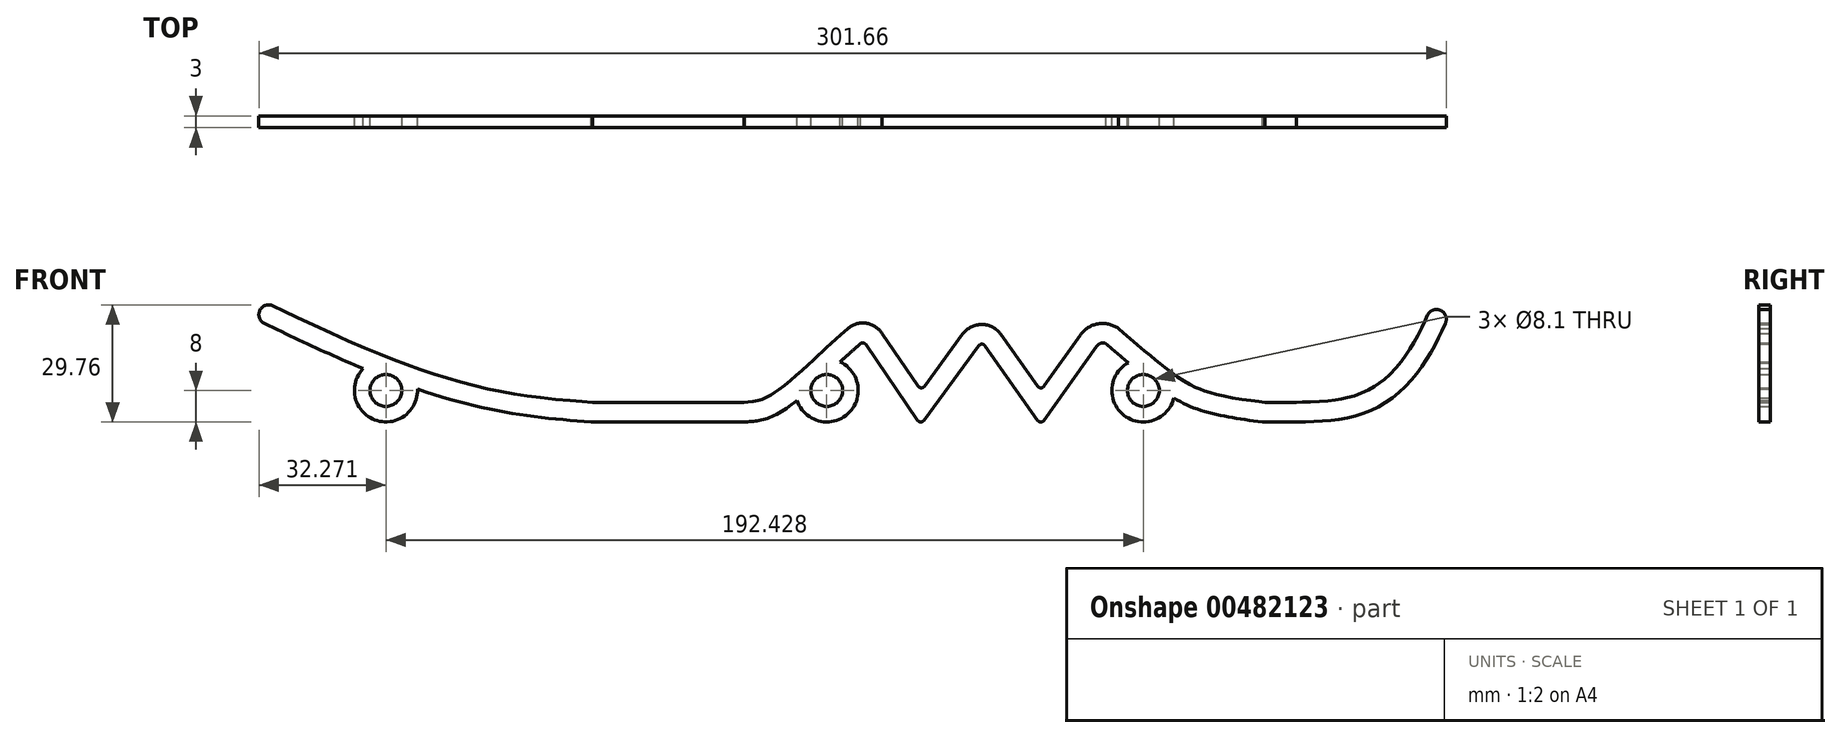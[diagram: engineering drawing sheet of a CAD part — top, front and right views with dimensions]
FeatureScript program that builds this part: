
annotation { "Feature Type Name" : "Feature", "Feature Type Description" : "" }
export const myFeature = defineFeature(function(context is Context, id is Id, definition is map)
    precondition{}
    {
        {
            var Q0;
            Q0=qCreatedBy(makeId("Front.planeOp"),FACE);
            var sketch = newSketch(context, id + "F0", { "sketchPlane" : qUnion([Q0])});
            skLineSegment(sketch, "E0.bottom", {"start": v(-221.82, -6.7) * mm, "end": v(78.18, -6.7) * mm, "construction": true});
            skLineSegment(sketch, "E0.top", {"start": v(-221.82, -36.7) * mm, "end": v(78.18, -36.7) * mm, "construction": true});
            skLineSegment(sketch, "E0.left", {"start": v(-221.82, -6.7) * mm, "end": v(-221.82, -36.7) * mm, "construction": true});
            skLineSegment(sketch, "E0.right", {"start": v(78.18, -6.7) * mm, "end": v(78.18, -36.7) * mm, "construction": true});
            skCircle(sketch, "E1", {"center": v(-190.97, -28.7) * mm, "radius": 4.05 * mm});
            skCircle(sketch, "E2", {"center": v(1.46, -28.7) * mm, "radius": 4.05 * mm});
            skLineSegment(sketch, "E3", {"start": v(-69, -17.05) * mm, "end": v(-55.9, -36.25) * mm});
            skLineSegment(sketch, "E4", {"start": v(-54.27, -36.28) * mm, "end": v(-40.4, -17.34) * mm});
            skLineSegment(sketch, "E5", {"start": v(-38.77, -17.36) * mm, "end": v(-25.39, -36.27) * mm});
            skLineSegment(sketch, "E6", {"start": v(-23.76, -36.27) * mm, "end": v(-10.46, -17.47) * mm});
            skLineSegment(sketch, "E7", {"start": v(-131.69, -16.22) * mm, "end": v(39.4, -16.22) * mm, "construction": true});
            skPoint(sketch, "E8.visualSharp", {"position": v(-99.57, -36.7) * mm});
            skPoint(sketch, "E9.visualSharp", {"position": v(-54.57, -36.7) * mm});
            skArc(sketch, "E9.filletArc", {"start": v(-55.9, -36.25) * mm, "mid": v(-55.1, -36.7) * mm, "end": v(-54.27, -36.28) * mm});
            skPoint(sketch, "E10.visualSharp", {"position": v(-24.57, -37.42) * mm});
            skArc(sketch, "E10.filletArc", {"start": v(-25.39, -36.27) * mm, "mid": v(-24.57, -36.7) * mm, "end": v(-23.76, -36.27) * mm});
            skPoint(sketch, "E11.visualSharp", {"position": v(48.18, -37.4) * mm});
            skPoint(sketch, "E12.visualSharp", {"position": v(-69.57, -16.22) * mm});
            skArc(sketch, "E12.filletArc", {"start": v(-69, -17.05) * mm, "mid": v(-69.65, -16.63) * mm, "end": v(-70.4, -16.79) * mm});
            skPoint(sketch, "E13.visualSharp", {"position": v(-39.57, -16.22) * mm});
            skArc(sketch, "E13.filletArc", {"start": v(-38.77, -17.36) * mm, "mid": v(-39.58, -16.93) * mm, "end": v(-40.4, -17.34) * mm});
            skPoint(sketch, "E14.visualSharp", {"position": v(-9.57, -16.22) * mm});
            skArc(sketch, "E14.filletArc", {"start": v(-8.14, -16.75) * mm, "mid": v(-9.42, -16.72) * mm, "end": v(-10.46, -17.47) * mm});
            skFitSpline(sketch, "E15", {"points": [v(-99.57, -36.7) * mm, v(-91.71, -34.76) * mm, v(-77.03, -22.8) * mm, v(-70.4, -16.79) * mm], "startDerivative": vector(26.04, 1.86) * mm, "endDerivative": vector(19.53, 17.39) * mm});
            skPoint(sketch, "E16", {"position": v(-221.82, -11.7) * mm});
            skFitSpline(sketch, "E17", {"points": [v(-221.82, -11.7) * mm, v(-189.76, -25.94) * mm, v(-161.24, -34.12) * mm, v(-138.8, -36.7) * mm], "startDerivative": vector(87.44, -41.7) * mm, "endDerivative": vector(74.23, -5.74) * mm});
            skLineSegment(sketch, "E18", {"start": v(-138.8, -36.7) * mm, "end": v(-99.57, -36.7) * mm});
            skFitSpline(sketch, "E19.0", {"points": [v(-219.67, -7.18) * mm, v(-216.02, -8.91) * mm, v(-208.76, -12.38) * mm, v(-199.77, -16.46) * mm, v(-192.64, -19.46) * mm, v(-187.34, -21.54) * mm, v(-182.05, -23.43) * mm, v(-176.82, -25.14) * mm, v(-171.66, -26.63) * mm, v(-166.6, -27.92) * mm, v(-161.68, -28.98) * mm, v(-156.92, -29.81) * mm, v(-152.25, -30.45) * mm, v(-146.1, -31.11) * mm, v(-141.51, -31.47) * mm, v(-138.42, -31.7) * mm]});
            skArc(sketch, "E20", {"start": v(-219.67, -7.18) * mm, "mid": v(-223, -8.36) * mm, "end": v(-221.82, -11.7) * mm});
            skFitSpline(sketch, "E21.0", {"points": [v(-99.93, -31.7) * mm, v(-99.39, -31.66) * mm, v(-98.4, -31.6) * mm, v(-97.13, -31.43) * mm, v(-96.16, -31.2) * mm, v(-95.35, -30.93) * mm, v(-94.81, -30.71) * mm, v(-94.35, -30.5) * mm, v(-94, -30.31) * mm, v(-93.62, -30.1) * mm, v(-93.07, -29.78) * mm, v(-92.33, -29.3) * mm, v(-91.05, -28.42) * mm, v(-89.33, -27.1) * mm, v(-87.18, -25.3) * mm, v(-85.02, -23.39) * mm, v(-82.93, -21.46) * mm, v(-81.29, -19.94) * mm, v(-80.07, -18.8) * mm, v(-78.93, -17.75) * mm, v(-77.63, -16.56) * mm, v(-76.24, -15.3) * mm, v(-74.95, -14.14) * mm, v(-74.13, -13.41) * mm, v(-73.72, -13.05) * mm]});
            skLineSegment(sketch, "E22", {"start": v(-138.42, -31.7) * mm, "end": v(-99.93, -31.7) * mm});
            skLineSegment(sketch, "E23.0", {"start": v(-64.88, -14.23) * mm, "end": v(-55.76, -27.6) * mm});
            skLineSegment(sketch, "E24.0", {"start": v(-34.69, -14.47) * mm, "end": v(-25.39, -27.61) * mm});
            skPoint(sketch, "E25", {"position": v(78.18, -11.7) * mm});
            skFitSpline(sketch, "E26", {"points": [v(78.18, -11.7) * mm, v(72.65, -21.98) * mm, v(63.85, -31.21) * mm, v(52.84, -35.72) * mm, v(40.46, -36.7) * mm], "startDerivative": vector(-20.1, -42.6) * mm, "endDerivative": vector(-49.74, -1.11) * mm});
            skFitSpline(sketch, "E27", {"points": [v(-8.14, -16.75) * mm, v(2.09, -25.34) * mm, v(13.73, -32.89) * mm, v(31.66, -36.7) * mm], "startDerivative": vector(32.38, -27.59) * mm, "endDerivative": vector(52.08, -6.85) * mm});
            skLineSegment(sketch, "E28", {"start": v(31.66, -36.7) * mm, "end": v(40.46, -36.7) * mm});
            skFitSpline(sketch, "E29.0", {"points": [v(-4.9, -12.94) * mm, v(-3.54, -14.1) * mm, v(-1.53, -15.81) * mm, v(1.17, -18.08) * mm, v(2.85, -19.5) * mm, v(4.2, -20.6) * mm, v(5.22, -21.44) * mm, v(6.24, -22.27) * mm, v(7.57, -23.33) * mm, v(9.22, -24.6) * mm, v(11.2, -25.96) * mm, v(12.9, -26.96) * mm, v(14.28, -27.67) * mm, v(15.17, -28.08) * mm, v(15.9, -28.37) * mm, v(16.65, -28.66) * mm, v(17.64, -29) * mm, v(18.89, -29.38) * mm, v(20.64, -29.84) * mm, v(22.97, -30.34) * mm, v(25.95, -30.85) * mm, v(29.08, -31.3) * mm, v(31.22, -31.6) * mm, v(32.3, -31.73) * mm]});
            skFitSpline(sketch, "E30.0", {"points": [v(73.66, -9.56) * mm, v(73.24, -10.44) * mm, v(72.42, -12.19) * mm, v(71.17, -14.7) * mm, v(70.07, -16.7) * mm, v(69.13, -18.25) * mm, v(68.14, -19.76) * mm, v(66.78, -21.61) * mm, v(64.97, -23.7) * mm, v(63.36, -25.25) * mm, v(62.03, -26.35) * mm, v(61.02, -27.1) * mm, v(59.99, -27.77) * mm, v(58.56, -28.59) * mm, v(56.69, -29.46) * mm, v(54.7, -30.13) * mm, v(53.05, -30.57) * mm, v(51.79, -30.84) * mm, v(50.49, -31.06) * mm, v(48.7, -31.3) * mm, v(46.37, -31.5) * mm, v(43.43, -31.62) * mm, v(41.39, -31.67) * mm, v(40.35, -31.7) * mm]});
            skArc(sketch, "E31", {"start": v(73.66, -9.56) * mm, "mid": v(76.99, -8.36) * mm, "end": v(78.18, -11.7) * mm});
            skLineSegment(sketch, "E32", {"start": v(32.3, -31.73) * mm, "end": v(40.35, -31.7) * mm});
            skArc(sketch, "E33", {"start": v(-14.54, -14.58) * mm, "mid": v(-10.06, -11.76) * mm, "end": v(-4.9, -12.94) * mm});
            skArc(sketch, "E34", {"start": v(-34.69, -14.47) * mm, "mid": v(-39.54, -11.93) * mm, "end": v(-44.43, -14.39) * mm});
            skArc(sketch, "E35", {"start": v(-73.72, -13.05) * mm, "mid": v(-69.03, -11.61) * mm, "end": v(-64.88, -14.23) * mm});
            skLineSegment(sketch, "E36.trimOffspring", {"start": v(-54.13, -27.62) * mm, "end": v(-44.43, -14.39) * mm});
            skLineSegment(sketch, "E37.trimOffspring", {"start": v(-23.76, -27.61) * mm, "end": v(-14.54, -14.58) * mm});
            skPoint(sketch, "E38.visualSharp", {"position": v(-54.96, -28.76) * mm});
            skArc(sketch, "E38.filletArc", {"start": v(-55.76, -27.6) * mm, "mid": v(-54.95, -28.03) * mm, "end": v(-54.13, -27.62) * mm});
            skPoint(sketch, "E39.visualSharp", {"position": v(-24.57, -28.77) * mm});
            skArc(sketch, "E39.filletArc", {"start": v(-25.39, -27.61) * mm, "mid": v(-24.57, -28.03) * mm, "end": v(-23.76, -27.61) * mm});
            skArc(sketch, "E40", {"start": v(-2.35, -21.66) * mm, "mid": v(-3.43, -35.02) * mm, "end": v(9.23, -30.6) * mm});
            skArc(sketch, "E41", {"start": v(-196.74, -23.15) * mm, "mid": v(-193.8, -36.17) * mm, "end": v(-182.98, -28.37) * mm});
            skCircle(sketch, "E42", {"center": v(-78.97, -28.7) * mm, "radius": 4.05 * mm});
            skArc(sketch, "E43", {"start": v(-86.55, -31.25) * mm, "mid": v(-73.64, -34.66) * mm, "end": v(-75.57, -21.45) * mm});
            skFitSpline(sketch, "E44.trimOffspring", {"points": [v(-99.57, -36.7) * mm, v(-91.71, -34.76) * mm, v(-77.03, -22.8) * mm, v(-70.4, -16.79) * mm], "startDerivative": vector(26.04, 1.86) * mm, "endDerivative": vector(19.53, 17.39) * mm});
            skSolve(sketch);
        }
        {
            var Q0;
            Q0 = qSketchRegion(id + "F0", true);
            extrude(context, id + "F1", {"entities" : qUnion([Q0]), "depth" : 3 * mm});
        }
    });
